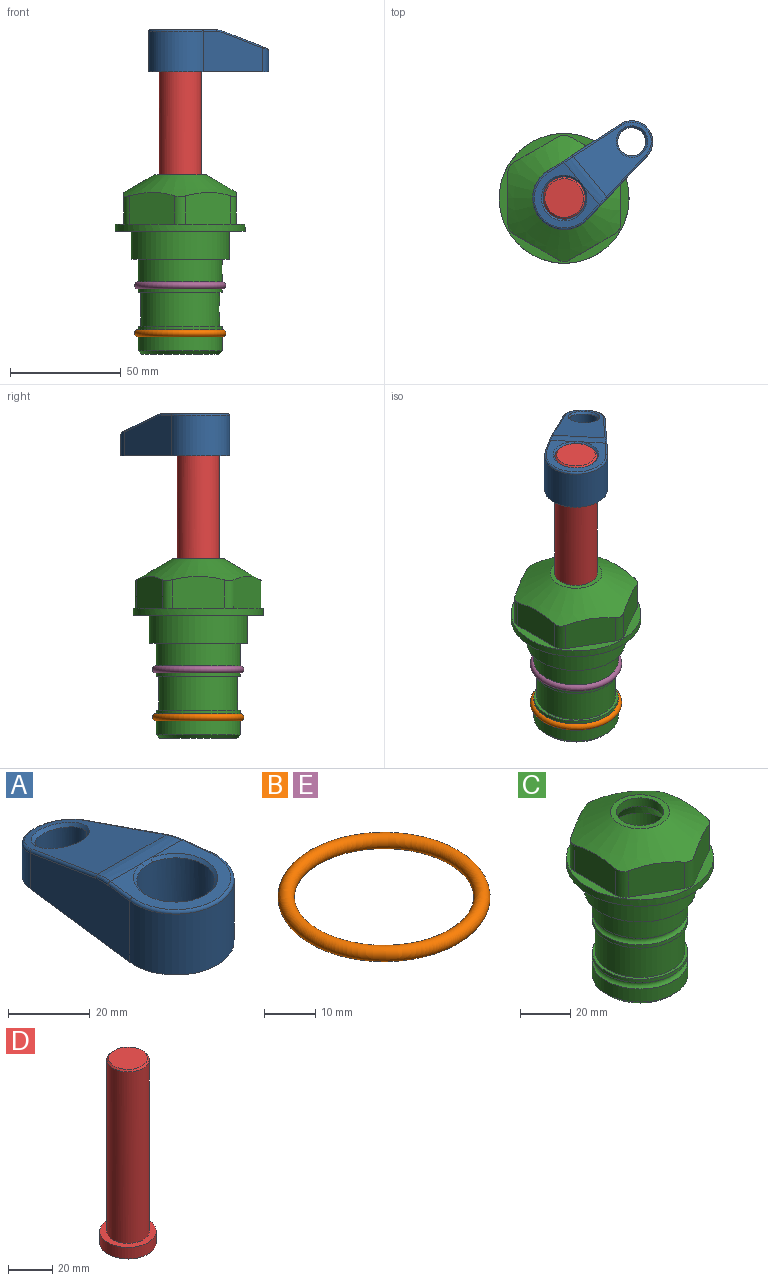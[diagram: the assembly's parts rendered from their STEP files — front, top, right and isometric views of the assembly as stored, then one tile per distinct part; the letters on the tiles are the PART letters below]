
ASSEMBLY  parts=5 mates=4
PART A: 31 faces, bbox 31.7x65.5x19.8 mm
  f0: plane 39.12x18.26mm, normal (0.99,0.12,0), area 612.2mm2, adj f1,f4,f7,f11,f13,f15
  f1: cylinder r=9.53mm len=18.91mm, axis (0,0,-1), area 296.1mm2, adj f0,f2,f7,f17
  f2: plane 39.12x18.26mm, normal (-0.99,0.12,0), area 612.2mm2, adj f1,f4,f7,f12,f14,f16
  f3: cylinder r=6.35mm len=12.7mm, axis (0,0,-1), area 362.4mm2, adj f7,f18
  f4: cylinder r=14.29mm len=28.58mm, axis (0,0,-1), area 882.2mm2, adj f0,f2,f7,f10
  f5: cylinder r=9.53mm len=19.05mm, axis (0,0,-1), area 1092.6mm2, adj f7,f19,f20
  f6: plane 26.99x23.69mm, normal (0,0,1), area 216.2mm2, adj f9,f10,f11,f12,f19
  f7: plane 63.5x28.58mm, normal (0,0,-1), area 661.8mm2, adj f0,f1,f2,f3,f4,f5,f22,f23
  f8: plane 33.52x23.6mm, normal (0,0.26,0.97), area 486mm2, adj f9,f15,f16,f17,f18
  f9: cylinder r=19.05mm len=24.72mm, axis (1,0,0), area 120.4mm2, adj f6,f8,f13,f14,f20
  f10: torus R=13.49mm, axis (0,0,1), area 59mm2, adj f4,f6,f11,f12
  f11: cylinder r=0.79mm len=8.67mm, axis (0.12,-0.99,0), area 10.8mm2, adj f0,f6,f10,f13
  f12: cylinder r=0.79mm len=8.67mm, axis (0.12,0.99,0), area 10.8mm2, adj f2,f6,f10,f14
  f13: bspline ~4.95x1.42mm, area 6.1mm2, adj f0,f9,f11,f15
  f14: bspline ~4.95x1.42mm, area 6.1mm2, adj f2,f9,f12,f16
  f15: cylinder r=0.79mm len=25.95mm, axis (0.12,-0.96,0.26), area 32.9mm2, adj f0,f8,f13,f17
  f16: cylinder r=0.79mm len=25.95mm, axis (0.12,0.96,-0.26), area 32.9mm2, adj f2,f8,f14,f17
  f17: bspline ~18.91x8.38mm, area 30mm2, adj f1,f8,f15,f16
  f18: bspline ~14.29x14.29mm, area 48.3mm2, adj f3,f8
  f19: cone r=9.53mm half-angle=45deg, axis (0,0,1), area 66.5mm2, adj f5,f6,f20
  f20: bspline ~3.22x0.96mm, area 3.5mm2, adj f5,f9,f19
  f21: plane 2.75x2.72mm, normal (0,0,-1), area 2.9mm2, adj f23,f25,f28
  f22: plane 23.05x15.88mm, normal (-0.99,-0.12,0), area 323.6mm2, adj f7,f25,f26,f27,f28,f29
  f23: plane 23.05x15.88mm, normal (0.99,-0.12,0), area 323.6mm2, adj f7,f21,f25,f27,f28,f30
  f24: cylinder r=9.53mm len=10.69mm, axis (0,0,-1), area 114.7mm2, adj f7,f27,f29,f30
  f25: cylinder r=12.7mm len=20.59mm, axis (0,0,-1), area 381.1mm2, adj f7,f21,f22,f23,f26,f28
  f26: plane 2.75x2.72mm, normal (0,0,-1), area 2.9mm2, adj f22,f25,f28
  f27: plane 19.72x18.37mm, normal (0,-0.26,-0.97), area 291.8mm2, adj f22,f23,f24,f28,f29,f30
  f28: cylinder r=15.88mm len=19.92mm, axis (1,0,0), area 54.8mm2, adj f21,f22,f23,f25,f26,f27
  f29: cylinder r=1.59mm len=11mm, axis (0,0,-1), area 34.7mm2, adj f7,f22,f24,f27
  f30: cylinder r=1.59mm len=11mm, axis (0,0,-1), area 34.7mm2, adj f7,f23,f24,f27
PART B: 1 faces, bbox 44.7x44.7x3.2 mm
  f0: torus R=19.05mm, axis (0,0,1), area 1193.9mm2
PART C: 36 faces, bbox 58.7x58.7x81 mm
  f0: cylinder r=17.78mm len=35.56mm, axis (0,0,1), area 1670.8mm2, adj f23,f24,f31
  f1: cylinder r=19.05mm len=38.1mm, axis (0,0,1), area 1191.9mm2, adj f26,f27,f30
  f2: plane 58.66x58.66mm, normal (0,0,-1), area 1150.6mm2, adj f3,f28
  f3: cylinder r=29.33mm len=58.66mm, axis (0,0,-1), area 585.1mm2, adj f2,f4
  f4: plane 58.66x58.66mm, normal (0,0,1), area 475.9mm2, adj f3,f5,f6,f7,f8,f9,f10,f11
  f5: plane 20.32x14.34mm, normal (-0.5,0.87,0), area 324.4mm2, adj f4,f15,f16,f17
  f6: plane 20.32x14.34mm, normal (0.5,0.87,0), area 324.4mm2, adj f4,f14,f15,f17
  f7: plane 23.48x14.34mm, normal (1,0,0), area 324.4mm2, adj f4,f13,f14,f17
  f8: plane 20.32x14.34mm, normal (0.5,-0.87,0), area 324.4mm2, adj f4,f12,f13,f17
  f9: plane 20.32x14.34mm, normal (-0.5,-0.87,0), area 324.4mm2, adj f4,f11,f12,f17
  f10: plane 23.48x14.34mm, normal (-1,0,0), area 324.4mm2, adj f4,f11,f16,f17
  f11: cylinder r=5.08mm len=12.85mm, axis (0,0,-1), area 67.2mm2, adj f4,f9,f10,f17
  f12: cylinder r=5.08mm len=12.85mm, axis (0,0,-1), area 67.2mm2, adj f4,f8,f9,f17
  f13: cylinder r=5.08mm len=12.85mm, axis (0,0,-1), area 67.2mm2, adj f4,f7,f8,f17
  f14: cylinder r=5.08mm len=12.85mm, axis (0,0,-1), area 67.2mm2, adj f4,f6,f7,f17
  f15: cylinder r=5.08mm len=12.85mm, axis (0,0,-1), area 67.2mm2, adj f4,f5,f6,f17
  f16: cylinder r=5.08mm len=12.85mm, axis (0,0,-1), area 67.2mm2, adj f4,f5,f10,f17
  f17: cone r=11.73mm half-angle=60deg, axis (0,0,-1), area 2071.8mm2, adj f5,f6,f7,f8,f9,f10,f11,f12
  f18: plane 23.46x23.46mm, normal (0,0,1), area 147.4mm2, adj f17,f35
  f19: plane 34.93x34.93mm, normal (0,0,-1), area 958mm2, adj f29
  f20: cylinder r=19.05mm len=38.1mm, axis (0,0,1), area 760.1mm2, adj f21,f29
  f21: torus R=19.05mm, axis (0,0,1), area 565.3mm2, adj f20,f22
  f22: cylinder r=19.05mm len=38.1mm, axis (0,0,1), area 190mm2, adj f21,f23
  f23: plane 38.1x38.1mm, normal (0,0,1), area 146.9mm2, adj f0,f22
  f24: plane 38.1x38.1mm, normal (0,0,-1), area 146.9mm2, adj f0,f25
  f25: cylinder r=19.05mm len=38.1mm, axis (0,0,1), area 190mm2, adj f24,f26
  f26: torus R=19.05mm, axis (0,0,1), area 565.3mm2, adj f1,f25
  f27: plane 44.45x44.45mm, normal (0,0,-1), area 411.7mm2, adj f1,f28
  f28: cylinder r=22.23mm len=44.45mm, axis (0,0,1), area 1773.5mm2, adj f2,f27
  f29: cone r=19.05mm half-angle=45deg, axis (0,0,1), area 257.5mm2, adj f19,f20
  f30: cylinder r=3.17mm len=6.75mm, axis (-1,0,0), area 128mm2, adj f1,f33
  f31: cylinder r=3.17mm len=6.35mm, axis (-1,0,0), area 102.5mm2, adj f0,f33
  f32: plane 25.4x25.4mm, normal (0,0,1), area 506.7mm2, adj f33
  f33: cylinder r=12.7mm len=66.42mm, axis (0,0,-1), area 5236.2mm2, adj f30,f31,f32,f34
  f34: cone r=9.53mm half-angle=30deg, axis (0,0,-1), area 443.4mm2, adj f33,f35
  f35: cylinder r=9.53mm len=19.05mm, axis (0,0,-1), area 240.9mm2, adj f18,f34
PART D: 6 faces, bbox 25.4x25.4x101.6 mm
  f0: plane 17.46x17.46mm, normal (0,0,1), area 239.5mm2, adj f5
  f1: plane 25.4x25.4mm, normal (0,0,-1), area 506.7mm2, adj f2
  f2: cylinder r=12.7mm len=25.4mm, axis (0,0,1), area 506.7mm2, adj f1,f3
  f3: plane 25.4x25.4mm, normal (0,0,1), area 221.7mm2, adj f2,f4
  f4: cylinder r=9.53mm len=94.46mm, axis (0,0,1), area 5653mm2, adj f3,f5
  f5: cone r=8.73mm half-angle=45deg, axis (0,0,-1), area 64.4mm2, adj f0,f4
PART E: same geometry as B
PLACE A rot(axis=(0,0,-1),50.2deg) t=(0,0,27.55)mm
PLACE B t=(0,0,-21.59)mm
PLACE C at identity fixed
PLACE D rot(axis=(0,0,-1),50.2deg) t=(0,0,27.55)mm
PLACE E at identity
MATE fastened E.f0 <-> C.f0  axis (0,0,1) through (0,0,-24.51)mm
MATE cylindrical C.f0 <-> D.f2  axis (0,0,1) through (0,0,-50.55)mm
MATE fastened D.f2 <-> A.f4  axis (0,0,1) through (0,0,91.05)mm
MATE fastened B.f0 <-> C.f0  axis (0,0,1) through (0,0,-46.1)mm
